# Revit family: Font_Sofa_Radius_360_Offecct
name_source: partatom
category: Furniture
revit_build: Autodesk Revit 2016 (Build: 20150714_1515(x64)
units: mm (PartAtom-declared; Revit-internal decimal feet)

## family parameters
Always vertical = Yes
Cut with Voids When Loaded = No
OmniClass Number = 23.40.20.14.14.14
OmniClass Title = Settees, Sofas
Room Calculation Point = No
Shared = No
Work Plane-Based = No

## types (1)
- Font_Sofa_Radius_360_Offecct
    AssetType = Movable
    BIMObjectName = Font_Sofa_Radius_360_Offecct
    Brand = Offecct
    Category = Sofa
    Color = Multiple
    ConvergoRefNr = 0019-1812-0003-SE
    Cost = 0 $
    Designer = Matti Klenell
    DurationUnit = Year
    HighestSeatingHeight = 460 mm  [stored 1.50919 ft]
    IfcExportAs = IfcFurnishingElementType
    IfcExportType = SOFA
    LowestSeatingHeight = 460 mm  [stored 1.50919 ft]
    MainColor = Various
    Manufacturer = Offecct
    ManufacturerName = Offecct
    ManufacturerURL = https://www.offecct.com
    Material = Steel & fabric
    Model = Font sofa radius 360
    Name = Font sofa radius 360
    NominalDepth = 2547 mm
    NominalHeight = 755 mm  [stored 2.47703 ft]
    NominalLength = 2730 mm  [stored 8.95669 ft]
    SeatingHeight = 460 mm  [stored 1.50919 ft]
    Shape = Sculptured
    Size = 2730x2547x755 mm
    URL = https://www.offecct.com
    Uniclass2 = Pr_40_50_12_81
    Uniclass2015Description = Sofas
    Uniclass2015Reference = Pr_40_50_12_81
    Version = 1
    VersionDate = 19/12/2018
    WarrantyDurationUnit = Year

note: [stored X ft] marks values corroborated as IEEE doubles in the binary element streams (Revit-internal decimal feet)

## geometry (parser evidence)
native form markers: Sweep x5
no freeform markers — native parametric forms only
